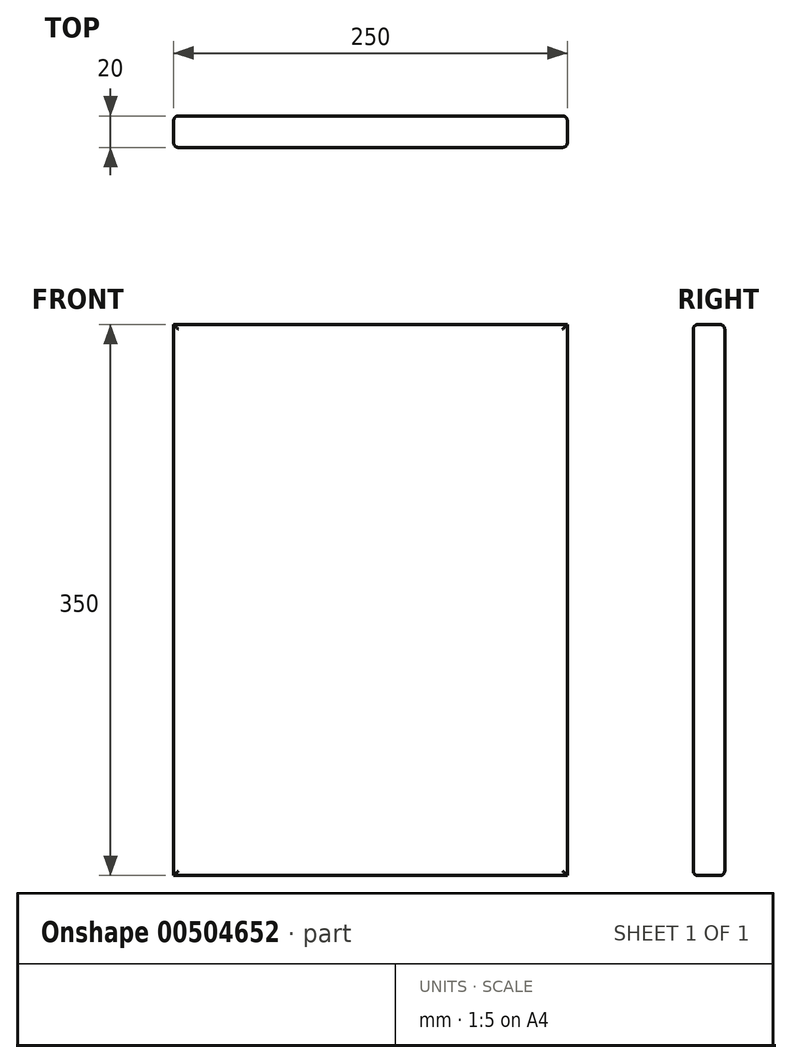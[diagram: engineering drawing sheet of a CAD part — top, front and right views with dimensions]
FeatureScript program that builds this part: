
annotation { "Feature Type Name" : "Feature", "Feature Type Description" : "" }
export const myFeature = defineFeature(function(context is Context, id is Id, definition is map)
    precondition{}
    {
        {
            var Q0;
            Q0=qCreatedBy(makeId("Front.planeOp"),FACE);
            var sketch = newSketch(context, id + "F0", { "sketchPlane" : qUnion([Q0])});
            skLineSegment(sketch, "E0.bottom", {"start": v(-202.07, 193.76) * mm, "end": v(47.93, 193.76) * mm});
            skLineSegment(sketch, "E0.top", {"start": v(-202.07, -156.24) * mm, "end": v(47.93, -156.24) * mm});
            skLineSegment(sketch, "E0.left", {"start": v(-202.07, 193.76) * mm, "end": v(-202.07, -156.24) * mm});
            skLineSegment(sketch, "E0.right", {"start": v(47.93, 193.76) * mm, "end": v(47.93, -156.24) * mm});
            skSolve(sketch);
        }
        {
            var Q0;
            Q0=makeQuery(id+"F0.imprint","IMPRINT",FACE,{"disambiguationData":[TD([[makeQuery(id+"F0.imprint","IMPRINT",EDGE,{"derivedFrom":sQuery(id+"F0.wireOp",EDGE,"E0.bottom")}),-1.0]])]});
            extrude(context, id + "F1", {"entities" : qUnion([Q0]), "depth" : 20 * mm});
        }
        {
            var Q0;
            Q0=makeQuery(id+"F1.opExtrude","SWEPT_FACE",FACE,{"disambiguationData":[OSD([sQuery(id+"F0.wireOp",EDGE,"E0.bottom")])]});
            var sketch = newSketch(context, id + "F2", { "sketchPlane" : qUnion([Q0])});
            skLineSegment(sketch, "E1", {"start": v(-202.07, 0) * mm, "end": v(-202.07, -10) * mm});
            skLineSegment(sketch, "E2", {"start": v(-202.07, -10) * mm, "end": v(-152.07, -10) * mm});
            skLineSegment(sketch, "E3", {"start": v(-152.07, -10) * mm, "end": v(-2.07, -10) * mm});
            skLineSegment(sketch, "E4", {"start": v(-2.07, -10) * mm, "end": v(47.93, -10) * mm});
            skSolve(sketch);
        }
        {
            var Q0;
            Q0=makeQuery(id+"F1.opExtrude","SWEPT_FACE",FACE,{"disambiguationData":[OSD([sQuery(id+"F0.wireOp",EDGE,"E0.top")])]});
            var sketch = newSketch(context, id + "F3", { "sketchPlane" : qUnion([Q0])});
            skLineSegment(sketch, "E5", {"start": v(-202.07, 10) * mm, "end": v(-152.07, 10) * mm});
            skLineSegment(sketch, "E6", {"start": v(-152.07, 10) * mm, "end": v(-2.07, 10) * mm});
            skLineSegment(sketch, "E7", {"start": v(-2.07, 10) * mm, "end": v(47.93, 10) * mm});
            skSolve(sketch);
        }
        {
            var Q0;
            Q0=makeQuery(id+"F1.opExtrude","CAP_FACE",FACE,{"disambiguationData":[OSD([sQuery(id+"F0.wireOp",EDGE,"E0.bottom"),sQuery(id+"F0.wireOp",EDGE,"E0.top"),sQuery(id+"F0.wireOp",EDGE,"E0.left"),sQuery(id+"F0.wireOp",EDGE,"E0.right")])],"isStart":false});
            var Q1;
            Q1=makeQuery(id+"F1.opExtrude","CAP_FACE",FACE,{"disambiguationData":[OSD([sQuery(id+"F0.wireOp",EDGE,"E0.bottom"),sQuery(id+"F0.wireOp",EDGE,"E0.top"),sQuery(id+"F0.wireOp",EDGE,"E0.left"),sQuery(id+"F0.wireOp",EDGE,"E0.right")])],"isStart":true});
            fillet(context, id + "F4", {"entities" : qUnion([Q0, Q1]), "radius" : 3 * mm, "tangentPropagation" : true, "allowEdgeOverflow" : false});
        }
    });
